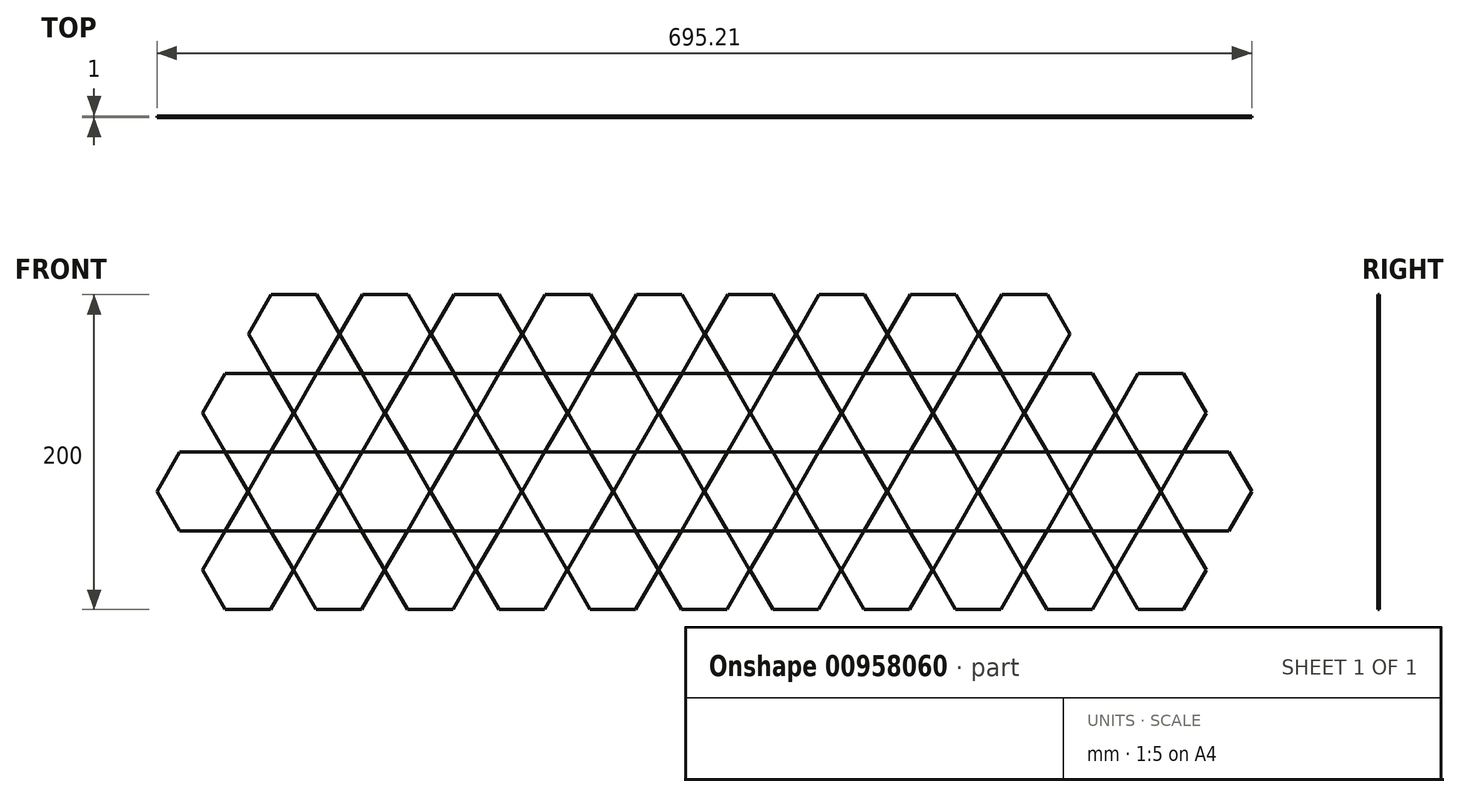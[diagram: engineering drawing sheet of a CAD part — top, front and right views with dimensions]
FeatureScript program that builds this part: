
annotation { "Feature Type Name" : "Feature", "Feature Type Description" : "" }
export const myFeature = defineFeature(function(context is Context, id is Id, definition is map)
    precondition{}
    {
        {
            var Q0;
            Q0=qCreatedBy(makeId("Front.planeOp"),FACE);
            var sketch = newSketch(context, id + "F0", { "sketchPlane" : qUnion([Q0])});
            skLineSegment(sketch, "E0.bottom", {"start": v(0, 0) * mm, "end": v(820, 0) * mm});
            skLineSegment(sketch, "E0.top", {"start": v(0, 215) * mm, "end": v(820, 215) * mm});
            skLineSegment(sketch, "E0.left", {"start": v(0, 0) * mm, "end": v(0, 215) * mm});
            skLineSegment(sketch, "E0.right", {"start": v(820, 0) * mm, "end": v(820, 215) * mm});
            skCircle(sketch, "E1.cCircle", {"center": v(39.24, 190) * mm, "radius": 25 * mm, "construction": true});
            skLineSegment(sketch, "E1.0", {"start": v(24.8, 215) * mm, "end": v(53.67, 215) * mm});
            skLineSegment(sketch, "E1.1", {"start": v(53.67, 215) * mm, "end": v(68.1, 190) * mm});
            skLineSegment(sketch, "E1.2", {"start": v(68.1, 190) * mm, "end": v(53.67, 165) * mm});
            skLineSegment(sketch, "E1.3", {"start": v(53.67, 165) * mm, "end": v(24.8, 165) * mm});
            skLineSegment(sketch, "E1.4", {"start": v(24.8, 165) * mm, "end": v(10.37, 190) * mm});
            skLineSegment(sketch, "E1.5", {"start": v(10.37, 190) * mm, "end": v(24.8, 215) * mm});
            skPoint(sketch, "E1.0.midPoint", {"position": v(39.24, 215) * mm});
            skCircle(sketch, "E2.cCircle", {"center": v(68.1, 140) * mm, "radius": 25 * mm, "construction": true});
            skLineSegment(sketch, "E2.0", {"start": v(53.67, 165) * mm, "end": v(82.54, 165) * mm});
            skLineSegment(sketch, "E2.1", {"start": v(82.54, 165) * mm, "end": v(96.97, 140) * mm});
            skLineSegment(sketch, "E2.2", {"start": v(96.97, 140) * mm, "end": v(82.54, 115) * mm});
            skLineSegment(sketch, "E2.3", {"start": v(82.54, 115) * mm, "end": v(53.67, 115) * mm});
            skLineSegment(sketch, "E2.4", {"start": v(53.67, 115) * mm, "end": v(39.24, 140) * mm});
            skLineSegment(sketch, "E2.5", {"start": v(39.24, 140) * mm, "end": v(53.67, 165) * mm});
            skPoint(sketch, "E2.0.midPoint", {"position": v(68.1, 165) * mm});
            skCircle(sketch, "E3.cCircle", {"center": v(96.97, 90) * mm, "radius": 25 * mm, "construction": true});
            skLineSegment(sketch, "E3.0", {"start": v(82.54, 115) * mm, "end": v(111.4, 115) * mm});
            skLineSegment(sketch, "E3.1", {"start": v(111.4, 115) * mm, "end": v(125.84, 90) * mm});
            skLineSegment(sketch, "E3.2", {"start": v(125.84, 90) * mm, "end": v(111.4, 65) * mm});
            skLineSegment(sketch, "E3.3", {"start": v(111.4, 65) * mm, "end": v(82.54, 65) * mm});
            skLineSegment(sketch, "E3.4", {"start": v(82.54, 65) * mm, "end": v(68.1, 90) * mm});
            skLineSegment(sketch, "E3.5", {"start": v(68.1, 90) * mm, "end": v(82.54, 115) * mm});
            skCircle(sketch, "E4.cCircle", {"center": v(125.84, 40) * mm, "radius": 25 * mm, "construction": true});
            skLineSegment(sketch, "E4.0", {"start": v(111.4, 65) * mm, "end": v(140.27, 65) * mm});
            skLineSegment(sketch, "E4.1", {"start": v(140.27, 65) * mm, "end": v(154.7, 40) * mm});
            skLineSegment(sketch, "E4.2", {"start": v(154.7, 40) * mm, "end": v(140.27, 15) * mm});
            skLineSegment(sketch, "E4.3", {"start": v(140.27, 15) * mm, "end": v(111.4, 15) * mm});
            skLineSegment(sketch, "E4.4", {"start": v(111.4, 15) * mm, "end": v(96.97, 40) * mm});
            skLineSegment(sketch, "E4.5", {"start": v(96.97, 40) * mm, "end": v(111.4, 65) * mm});
            skLineSegment(sketch, "E5", {"start": v(10.37, 190) * mm, "end": v(96.97, 40) * mm});
            skLineSegment(sketch, "E6.1.0.0", {"start": v(198.27, 65) * mm, "end": v(212.7, 40) * mm});
            skCircle(sketch, "E6.1.0.1", {"center": v(126.1, 140) * mm, "radius": 25 * mm, "construction": true});
            skLineSegment(sketch, "E6.1.0.2", {"start": v(126.1, 190) * mm, "end": v(111.67, 165) * mm});
            skPoint(sketch, "E6.1.0.4", {"position": v(97.24, 215) * mm});
            skLineSegment(sketch, "E6.1.0.5", {"start": v(111.67, 115) * mm, "end": v(97.24, 140) * mm});
            skLineSegment(sketch, "E6.1.0.6", {"start": v(140.54, 65) * mm, "end": v(126.1, 90) * mm});
            skLineSegment(sketch, "E6.1.0.7", {"start": v(140.54, 165) * mm, "end": v(154.97, 140) * mm});
            skLineSegment(sketch, "E6.1.0.8", {"start": v(111.67, 215) * mm, "end": v(126.1, 190) * mm});
            skCircle(sketch, "E6.1.0.9", {"center": v(154.97, 90) * mm, "radius": 25 * mm, "construction": true});
            skCircle(sketch, "E6.1.0.10", {"center": v(97.24, 190) * mm, "radius": 25 * mm, "construction": true});
            skLineSegment(sketch, "E6.1.0.11", {"start": v(82.8, 165) * mm, "end": v(68.37, 190) * mm});
            skLineSegment(sketch, "E6.1.0.12", {"start": v(97.24, 140) * mm, "end": v(111.67, 165) * mm});
            skLineSegment(sketch, "E6.1.0.13", {"start": v(183.84, 90) * mm, "end": v(169.4, 65) * mm});
            skLineSegment(sketch, "E6.1.0.14", {"start": v(68.37, 190) * mm, "end": v(154.97, 40) * mm});
            skPoint(sketch, "E6.1.0.15", {"position": v(126.1, 165) * mm});
            skCircle(sketch, "E6.1.0.16", {"center": v(183.84, 40) * mm, "radius": 25 * mm, "construction": true});
            skLineSegment(sketch, "E6.1.0.17", {"start": v(140.54, 115) * mm, "end": v(111.67, 115) * mm});
            skLineSegment(sketch, "E6.1.0.18", {"start": v(198.27, 15) * mm, "end": v(169.4, 15) * mm});
            skLineSegment(sketch, "E6.1.0.19", {"start": v(68.37, 190) * mm, "end": v(82.8, 215) * mm});
            skLineSegment(sketch, "E6.1.0.20", {"start": v(126.1, 90) * mm, "end": v(140.54, 115) * mm});
            skLineSegment(sketch, "E6.1.0.21", {"start": v(111.67, 165) * mm, "end": v(82.8, 165) * mm});
            skLineSegment(sketch, "E6.1.0.22", {"start": v(111.67, 165) * mm, "end": v(140.54, 165) * mm});
            skLineSegment(sketch, "E6.1.0.23", {"start": v(169.4, 65) * mm, "end": v(198.27, 65) * mm});
            skLineSegment(sketch, "E6.1.0.24", {"start": v(140.54, 115) * mm, "end": v(169.4, 115) * mm});
            skLineSegment(sketch, "E6.1.0.25", {"start": v(169.4, 115) * mm, "end": v(183.84, 90) * mm});
            skLineSegment(sketch, "E6.1.0.26", {"start": v(212.7, 40) * mm, "end": v(198.27, 15) * mm});
            skLineSegment(sketch, "E6.1.0.27", {"start": v(169.4, 15) * mm, "end": v(154.97, 40) * mm});
            skLineSegment(sketch, "E6.1.0.28", {"start": v(169.4, 65) * mm, "end": v(140.54, 65) * mm});
            skLineSegment(sketch, "E6.1.0.29", {"start": v(154.97, 140) * mm, "end": v(140.54, 115) * mm});
            skLineSegment(sketch, "E6.1.0.30", {"start": v(154.97, 40) * mm, "end": v(169.4, 65) * mm});
            skLineSegment(sketch, "E6.1.0.31", {"start": v(82.8, 215) * mm, "end": v(111.67, 215) * mm});
            skLineSegment(sketch, "E6.2.0.0", {"start": v(256.27, 65) * mm, "end": v(270.7, 40) * mm});
            skCircle(sketch, "E6.2.0.1", {"center": v(184.1, 140) * mm, "radius": 25 * mm, "construction": true});
            skLineSegment(sketch, "E6.2.0.2", {"start": v(184.1, 190) * mm, "end": v(169.67, 165) * mm});
            skPoint(sketch, "E6.2.0.4", {"position": v(155.24, 215) * mm});
            skLineSegment(sketch, "E6.2.0.5", {"start": v(169.67, 115) * mm, "end": v(155.24, 140) * mm});
            skLineSegment(sketch, "E6.2.0.6", {"start": v(198.54, 65) * mm, "end": v(184.1, 90) * mm});
            skLineSegment(sketch, "E6.2.0.7", {"start": v(198.54, 165) * mm, "end": v(212.97, 140) * mm});
            skLineSegment(sketch, "E6.2.0.8", {"start": v(169.67, 215) * mm, "end": v(184.1, 190) * mm});
            skCircle(sketch, "E6.2.0.9", {"center": v(212.97, 90) * mm, "radius": 25 * mm, "construction": true});
            skCircle(sketch, "E6.2.0.10", {"center": v(155.24, 190) * mm, "radius": 25 * mm, "construction": true});
            skLineSegment(sketch, "E6.2.0.11", {"start": v(140.8, 165) * mm, "end": v(126.37, 190) * mm});
            skLineSegment(sketch, "E6.2.0.12", {"start": v(155.24, 140) * mm, "end": v(169.67, 165) * mm});
            skLineSegment(sketch, "E6.2.0.13", {"start": v(241.84, 90) * mm, "end": v(227.4, 65) * mm});
            skLineSegment(sketch, "E6.2.0.14", {"start": v(126.37, 190) * mm, "end": v(212.97, 40) * mm});
            skPoint(sketch, "E6.2.0.15", {"position": v(184.1, 165) * mm});
            skCircle(sketch, "E6.2.0.16", {"center": v(241.84, 40) * mm, "radius": 25 * mm, "construction": true});
            skLineSegment(sketch, "E6.2.0.17", {"start": v(198.54, 115) * mm, "end": v(169.67, 115) * mm});
            skLineSegment(sketch, "E6.2.0.18", {"start": v(256.27, 15) * mm, "end": v(227.4, 15) * mm});
            skLineSegment(sketch, "E6.2.0.19", {"start": v(126.37, 190) * mm, "end": v(140.8, 215) * mm});
            skLineSegment(sketch, "E6.2.0.20", {"start": v(184.1, 90) * mm, "end": v(198.54, 115) * mm});
            skLineSegment(sketch, "E6.2.0.21", {"start": v(169.67, 165) * mm, "end": v(140.8, 165) * mm});
            skLineSegment(sketch, "E6.2.0.22", {"start": v(169.67, 165) * mm, "end": v(198.54, 165) * mm});
            skLineSegment(sketch, "E6.2.0.23", {"start": v(227.4, 65) * mm, "end": v(256.27, 65) * mm});
            skLineSegment(sketch, "E6.2.0.24", {"start": v(198.54, 115) * mm, "end": v(227.4, 115) * mm});
            skLineSegment(sketch, "E6.2.0.25", {"start": v(227.4, 115) * mm, "end": v(241.84, 90) * mm});
            skLineSegment(sketch, "E6.2.0.26", {"start": v(270.7, 40) * mm, "end": v(256.27, 15) * mm});
            skLineSegment(sketch, "E6.2.0.27", {"start": v(227.4, 15) * mm, "end": v(212.97, 40) * mm});
            skLineSegment(sketch, "E6.2.0.28", {"start": v(227.4, 65) * mm, "end": v(198.54, 65) * mm});
            skLineSegment(sketch, "E6.2.0.29", {"start": v(212.97, 140) * mm, "end": v(198.54, 115) * mm});
            skLineSegment(sketch, "E6.2.0.30", {"start": v(212.97, 40) * mm, "end": v(227.4, 65) * mm});
            skLineSegment(sketch, "E6.2.0.31", {"start": v(140.8, 215) * mm, "end": v(169.67, 215) * mm});
            skLineSegment(sketch, "E6.3.0.0", {"start": v(314.27, 65) * mm, "end": v(328.7, 40) * mm});
            skCircle(sketch, "E6.3.0.1", {"center": v(242.1, 140) * mm, "radius": 25 * mm, "construction": true});
            skLineSegment(sketch, "E6.3.0.2", {"start": v(242.1, 190) * mm, "end": v(227.67, 165) * mm});
            skPoint(sketch, "E6.3.0.4", {"position": v(213.24, 215) * mm});
            skLineSegment(sketch, "E6.3.0.5", {"start": v(227.67, 115) * mm, "end": v(213.24, 140) * mm});
            skLineSegment(sketch, "E6.3.0.6", {"start": v(256.54, 65) * mm, "end": v(242.1, 90) * mm});
            skLineSegment(sketch, "E6.3.0.7", {"start": v(256.54, 165) * mm, "end": v(270.97, 140) * mm});
            skLineSegment(sketch, "E6.3.0.8", {"start": v(227.67, 215) * mm, "end": v(242.1, 190) * mm});
            skCircle(sketch, "E6.3.0.9", {"center": v(270.97, 90) * mm, "radius": 25 * mm, "construction": true});
            skCircle(sketch, "E6.3.0.10", {"center": v(213.24, 190) * mm, "radius": 25 * mm, "construction": true});
            skLineSegment(sketch, "E6.3.0.11", {"start": v(198.8, 165) * mm, "end": v(184.37, 190) * mm});
            skLineSegment(sketch, "E6.3.0.12", {"start": v(213.24, 140) * mm, "end": v(227.67, 165) * mm});
            skLineSegment(sketch, "E6.3.0.13", {"start": v(299.84, 90) * mm, "end": v(285.4, 65) * mm});
            skLineSegment(sketch, "E6.3.0.14", {"start": v(184.37, 190) * mm, "end": v(270.97, 40) * mm});
            skPoint(sketch, "E6.3.0.15", {"position": v(242.1, 165) * mm});
            skCircle(sketch, "E6.3.0.16", {"center": v(299.84, 40) * mm, "radius": 25 * mm, "construction": true});
            skLineSegment(sketch, "E6.3.0.17", {"start": v(256.54, 115) * mm, "end": v(227.67, 115) * mm});
            skLineSegment(sketch, "E6.3.0.18", {"start": v(314.27, 15) * mm, "end": v(285.4, 15) * mm});
            skLineSegment(sketch, "E6.3.0.19", {"start": v(184.37, 190) * mm, "end": v(198.8, 215) * mm});
            skLineSegment(sketch, "E6.3.0.20", {"start": v(242.1, 90) * mm, "end": v(256.54, 115) * mm});
            skLineSegment(sketch, "E6.3.0.21", {"start": v(227.67, 165) * mm, "end": v(198.8, 165) * mm});
            skLineSegment(sketch, "E6.3.0.22", {"start": v(227.67, 165) * mm, "end": v(256.54, 165) * mm});
            skLineSegment(sketch, "E6.3.0.23", {"start": v(285.4, 65) * mm, "end": v(314.27, 65) * mm});
            skLineSegment(sketch, "E6.3.0.24", {"start": v(256.54, 115) * mm, "end": v(285.4, 115) * mm});
            skLineSegment(sketch, "E6.3.0.25", {"start": v(285.4, 115) * mm, "end": v(299.84, 90) * mm});
            skLineSegment(sketch, "E6.3.0.26", {"start": v(328.7, 40) * mm, "end": v(314.27, 15) * mm});
            skLineSegment(sketch, "E6.3.0.27", {"start": v(285.4, 15) * mm, "end": v(270.97, 40) * mm});
            skLineSegment(sketch, "E6.3.0.28", {"start": v(285.4, 65) * mm, "end": v(256.54, 65) * mm});
            skLineSegment(sketch, "E6.3.0.29", {"start": v(270.97, 140) * mm, "end": v(256.54, 115) * mm});
            skLineSegment(sketch, "E6.3.0.30", {"start": v(270.97, 40) * mm, "end": v(285.4, 65) * mm});
            skLineSegment(sketch, "E6.3.0.31", {"start": v(198.8, 215) * mm, "end": v(227.67, 215) * mm});
            skLineSegment(sketch, "E6.4.0.0", {"start": v(372.27, 65) * mm, "end": v(386.7, 40) * mm});
            skCircle(sketch, "E6.4.0.1", {"center": v(300.1, 140) * mm, "radius": 25 * mm, "construction": true});
            skLineSegment(sketch, "E6.4.0.2", {"start": v(300.1, 190) * mm, "end": v(285.67, 165) * mm});
            skPoint(sketch, "E6.4.0.4", {"position": v(271.24, 215) * mm});
            skLineSegment(sketch, "E6.4.0.5", {"start": v(285.67, 115) * mm, "end": v(271.24, 140) * mm});
            skLineSegment(sketch, "E6.4.0.6", {"start": v(314.54, 65) * mm, "end": v(300.1, 90) * mm});
            skLineSegment(sketch, "E6.4.0.7", {"start": v(314.54, 165) * mm, "end": v(328.97, 140) * mm});
            skLineSegment(sketch, "E6.4.0.8", {"start": v(285.67, 215) * mm, "end": v(300.1, 190) * mm});
            skCircle(sketch, "E6.4.0.9", {"center": v(328.97, 90) * mm, "radius": 25 * mm, "construction": true});
            skCircle(sketch, "E6.4.0.10", {"center": v(271.24, 190) * mm, "radius": 25 * mm, "construction": true});
            skLineSegment(sketch, "E6.4.0.11", {"start": v(256.8, 165) * mm, "end": v(242.37, 190) * mm});
            skLineSegment(sketch, "E6.4.0.12", {"start": v(271.24, 140) * mm, "end": v(285.67, 165) * mm});
            skLineSegment(sketch, "E6.4.0.13", {"start": v(357.84, 90) * mm, "end": v(343.4, 65) * mm});
            skLineSegment(sketch, "E6.4.0.14", {"start": v(242.37, 190) * mm, "end": v(328.97, 40) * mm});
            skPoint(sketch, "E6.4.0.15", {"position": v(300.1, 165) * mm});
            skCircle(sketch, "E6.4.0.16", {"center": v(357.84, 40) * mm, "radius": 25 * mm, "construction": true});
            skLineSegment(sketch, "E6.4.0.17", {"start": v(314.54, 115) * mm, "end": v(285.67, 115) * mm});
            skLineSegment(sketch, "E6.4.0.18", {"start": v(372.27, 15) * mm, "end": v(343.4, 15) * mm});
            skLineSegment(sketch, "E6.4.0.19", {"start": v(242.37, 190) * mm, "end": v(256.8, 215) * mm});
            skLineSegment(sketch, "E6.4.0.20", {"start": v(300.1, 90) * mm, "end": v(314.54, 115) * mm});
            skLineSegment(sketch, "E6.4.0.21", {"start": v(285.67, 165) * mm, "end": v(256.8, 165) * mm});
            skLineSegment(sketch, "E6.4.0.22", {"start": v(285.67, 165) * mm, "end": v(314.54, 165) * mm});
            skLineSegment(sketch, "E6.4.0.23", {"start": v(343.4, 65) * mm, "end": v(372.27, 65) * mm});
            skLineSegment(sketch, "E6.4.0.24", {"start": v(314.54, 115) * mm, "end": v(343.4, 115) * mm});
            skLineSegment(sketch, "E6.4.0.25", {"start": v(343.4, 115) * mm, "end": v(357.84, 90) * mm});
            skLineSegment(sketch, "E6.4.0.26", {"start": v(386.7, 40) * mm, "end": v(372.27, 15) * mm});
            skLineSegment(sketch, "E6.4.0.27", {"start": v(343.4, 15) * mm, "end": v(328.97, 40) * mm});
            skLineSegment(sketch, "E6.4.0.28", {"start": v(343.4, 65) * mm, "end": v(314.54, 65) * mm});
            skLineSegment(sketch, "E6.4.0.29", {"start": v(328.97, 140) * mm, "end": v(314.54, 115) * mm});
            skLineSegment(sketch, "E6.4.0.30", {"start": v(328.97, 40) * mm, "end": v(343.4, 65) * mm});
            skLineSegment(sketch, "E6.4.0.31", {"start": v(256.8, 215) * mm, "end": v(285.67, 215) * mm});
            skLineSegment(sketch, "E6.5.0.0", {"start": v(430.27, 65) * mm, "end": v(444.7, 40) * mm});
            skCircle(sketch, "E6.5.0.1", {"center": v(358.1, 140) * mm, "radius": 25 * mm, "construction": true});
            skLineSegment(sketch, "E6.5.0.2", {"start": v(358.1, 190) * mm, "end": v(343.67, 165) * mm});
            skPoint(sketch, "E6.5.0.4", {"position": v(329.24, 215) * mm});
            skLineSegment(sketch, "E6.5.0.5", {"start": v(343.67, 115) * mm, "end": v(329.24, 140) * mm});
            skLineSegment(sketch, "E6.5.0.6", {"start": v(372.54, 65) * mm, "end": v(358.1, 90) * mm});
            skLineSegment(sketch, "E6.5.0.7", {"start": v(372.54, 165) * mm, "end": v(386.97, 140) * mm});
            skLineSegment(sketch, "E6.5.0.8", {"start": v(343.67, 215) * mm, "end": v(358.1, 190) * mm});
            skCircle(sketch, "E6.5.0.9", {"center": v(386.97, 90) * mm, "radius": 25 * mm, "construction": true});
            skCircle(sketch, "E6.5.0.10", {"center": v(329.24, 190) * mm, "radius": 25 * mm, "construction": true});
            skLineSegment(sketch, "E6.5.0.11", {"start": v(314.8, 165) * mm, "end": v(300.37, 190) * mm});
            skLineSegment(sketch, "E6.5.0.12", {"start": v(329.24, 140) * mm, "end": v(343.67, 165) * mm});
            skLineSegment(sketch, "E6.5.0.13", {"start": v(415.84, 90) * mm, "end": v(401.4, 65) * mm});
            skLineSegment(sketch, "E6.5.0.14", {"start": v(300.37, 190) * mm, "end": v(386.97, 40) * mm});
            skPoint(sketch, "E6.5.0.15", {"position": v(358.1, 165) * mm});
            skCircle(sketch, "E6.5.0.16", {"center": v(415.84, 40) * mm, "radius": 25 * mm, "construction": true});
            skLineSegment(sketch, "E6.5.0.17", {"start": v(372.54, 115) * mm, "end": v(343.67, 115) * mm});
            skLineSegment(sketch, "E6.5.0.18", {"start": v(430.27, 15) * mm, "end": v(401.4, 15) * mm});
            skLineSegment(sketch, "E6.5.0.19", {"start": v(300.37, 190) * mm, "end": v(314.8, 215) * mm});
            skLineSegment(sketch, "E6.5.0.20", {"start": v(358.1, 90) * mm, "end": v(372.54, 115) * mm});
            skLineSegment(sketch, "E6.5.0.21", {"start": v(343.67, 165) * mm, "end": v(314.8, 165) * mm});
            skLineSegment(sketch, "E6.5.0.22", {"start": v(343.67, 165) * mm, "end": v(372.54, 165) * mm});
            skLineSegment(sketch, "E6.5.0.23", {"start": v(401.4, 65) * mm, "end": v(430.27, 65) * mm});
            skLineSegment(sketch, "E6.5.0.24", {"start": v(372.54, 115) * mm, "end": v(401.4, 115) * mm});
            skLineSegment(sketch, "E6.5.0.25", {"start": v(401.4, 115) * mm, "end": v(415.84, 90) * mm});
            skLineSegment(sketch, "E6.5.0.26", {"start": v(444.7, 40) * mm, "end": v(430.27, 15) * mm});
            skLineSegment(sketch, "E6.5.0.27", {"start": v(401.4, 15) * mm, "end": v(386.97, 40) * mm});
            skLineSegment(sketch, "E6.5.0.28", {"start": v(401.4, 65) * mm, "end": v(372.54, 65) * mm});
            skLineSegment(sketch, "E6.5.0.29", {"start": v(386.97, 140) * mm, "end": v(372.54, 115) * mm});
            skLineSegment(sketch, "E6.5.0.30", {"start": v(386.97, 40) * mm, "end": v(401.4, 65) * mm});
            skLineSegment(sketch, "E6.5.0.31", {"start": v(314.8, 215) * mm, "end": v(343.67, 215) * mm});
            skLineSegment(sketch, "E6.6.0.0", {"start": v(488.27, 65) * mm, "end": v(502.7, 40) * mm});
            skCircle(sketch, "E6.6.0.1", {"center": v(416.1, 140) * mm, "radius": 25 * mm, "construction": true});
            skLineSegment(sketch, "E6.6.0.2", {"start": v(416.1, 190) * mm, "end": v(401.67, 165) * mm});
            skPoint(sketch, "E6.6.0.4", {"position": v(387.24, 215) * mm});
            skLineSegment(sketch, "E6.6.0.5", {"start": v(401.67, 115) * mm, "end": v(387.24, 140) * mm});
            skLineSegment(sketch, "E6.6.0.6", {"start": v(430.54, 65) * mm, "end": v(416.1, 90) * mm});
            skLineSegment(sketch, "E6.6.0.7", {"start": v(430.54, 165) * mm, "end": v(444.97, 140) * mm});
            skLineSegment(sketch, "E6.6.0.8", {"start": v(401.67, 215) * mm, "end": v(416.1, 190) * mm});
            skCircle(sketch, "E6.6.0.9", {"center": v(444.97, 90) * mm, "radius": 25 * mm, "construction": true});
            skCircle(sketch, "E6.6.0.10", {"center": v(387.24, 190) * mm, "radius": 25 * mm, "construction": true});
            skLineSegment(sketch, "E6.6.0.11", {"start": v(372.8, 165) * mm, "end": v(358.37, 190) * mm});
            skLineSegment(sketch, "E6.6.0.12", {"start": v(387.24, 140) * mm, "end": v(401.67, 165) * mm});
            skLineSegment(sketch, "E6.6.0.13", {"start": v(473.84, 90) * mm, "end": v(459.4, 65) * mm});
            skLineSegment(sketch, "E6.6.0.14", {"start": v(358.37, 190) * mm, "end": v(444.97, 40) * mm});
            skPoint(sketch, "E6.6.0.15", {"position": v(416.1, 165) * mm});
            skCircle(sketch, "E6.6.0.16", {"center": v(473.84, 40) * mm, "radius": 25 * mm, "construction": true});
            skLineSegment(sketch, "E6.6.0.17", {"start": v(430.54, 115) * mm, "end": v(401.67, 115) * mm});
            skLineSegment(sketch, "E6.6.0.18", {"start": v(488.27, 15) * mm, "end": v(459.4, 15) * mm});
            skLineSegment(sketch, "E6.6.0.19", {"start": v(358.37, 190) * mm, "end": v(372.8, 215) * mm});
            skLineSegment(sketch, "E6.6.0.20", {"start": v(416.1, 90) * mm, "end": v(430.54, 115) * mm});
            skLineSegment(sketch, "E6.6.0.21", {"start": v(401.67, 165) * mm, "end": v(372.8, 165) * mm});
            skLineSegment(sketch, "E6.6.0.22", {"start": v(401.67, 165) * mm, "end": v(430.54, 165) * mm});
            skLineSegment(sketch, "E6.6.0.23", {"start": v(459.4, 65) * mm, "end": v(488.27, 65) * mm});
            skLineSegment(sketch, "E6.6.0.24", {"start": v(430.54, 115) * mm, "end": v(459.4, 115) * mm});
            skLineSegment(sketch, "E6.6.0.25", {"start": v(459.4, 115) * mm, "end": v(473.84, 90) * mm});
            skLineSegment(sketch, "E6.6.0.26", {"start": v(502.7, 40) * mm, "end": v(488.27, 15) * mm});
            skLineSegment(sketch, "E6.6.0.27", {"start": v(459.4, 15) * mm, "end": v(444.97, 40) * mm});
            skLineSegment(sketch, "E6.6.0.28", {"start": v(459.4, 65) * mm, "end": v(430.54, 65) * mm});
            skLineSegment(sketch, "E6.6.0.29", {"start": v(444.97, 140) * mm, "end": v(430.54, 115) * mm});
            skLineSegment(sketch, "E6.6.0.30", {"start": v(444.97, 40) * mm, "end": v(459.4, 65) * mm});
            skLineSegment(sketch, "E6.6.0.31", {"start": v(372.8, 215) * mm, "end": v(401.67, 215) * mm});
            skLineSegment(sketch, "E6.7.0.0", {"start": v(546.27, 65) * mm, "end": v(560.7, 40) * mm});
            skCircle(sketch, "E6.7.0.1", {"center": v(474.1, 140) * mm, "radius": 25 * mm, "construction": true});
            skLineSegment(sketch, "E6.7.0.2", {"start": v(474.1, 190) * mm, "end": v(459.67, 165) * mm});
            skPoint(sketch, "E6.7.0.4", {"position": v(445.24, 215) * mm});
            skLineSegment(sketch, "E6.7.0.5", {"start": v(459.67, 115) * mm, "end": v(445.24, 140) * mm});
            skLineSegment(sketch, "E6.7.0.6", {"start": v(488.54, 65) * mm, "end": v(474.1, 90) * mm});
            skLineSegment(sketch, "E6.7.0.7", {"start": v(488.54, 165) * mm, "end": v(502.97, 140) * mm});
            skLineSegment(sketch, "E6.7.0.8", {"start": v(459.67, 215) * mm, "end": v(474.1, 190) * mm});
            skCircle(sketch, "E6.7.0.9", {"center": v(502.97, 90) * mm, "radius": 25 * mm, "construction": true});
            skCircle(sketch, "E6.7.0.10", {"center": v(445.24, 190) * mm, "radius": 25 * mm, "construction": true});
            skLineSegment(sketch, "E6.7.0.11", {"start": v(430.8, 165) * mm, "end": v(416.37, 190) * mm});
            skLineSegment(sketch, "E6.7.0.12", {"start": v(445.24, 140) * mm, "end": v(459.67, 165) * mm});
            skLineSegment(sketch, "E6.7.0.13", {"start": v(531.84, 90) * mm, "end": v(517.4, 65) * mm});
            skLineSegment(sketch, "E6.7.0.14", {"start": v(416.37, 190) * mm, "end": v(502.97, 40) * mm});
            skPoint(sketch, "E6.7.0.15", {"position": v(474.1, 165) * mm});
            skCircle(sketch, "E6.7.0.16", {"center": v(531.84, 40) * mm, "radius": 25 * mm, "construction": true});
            skLineSegment(sketch, "E6.7.0.17", {"start": v(488.54, 115) * mm, "end": v(459.67, 115) * mm});
            skLineSegment(sketch, "E6.7.0.18", {"start": v(546.27, 15) * mm, "end": v(517.4, 15) * mm});
            skLineSegment(sketch, "E6.7.0.19", {"start": v(416.37, 190) * mm, "end": v(430.8, 215) * mm});
            skLineSegment(sketch, "E6.7.0.20", {"start": v(474.1, 90) * mm, "end": v(488.54, 115) * mm});
            skLineSegment(sketch, "E6.7.0.21", {"start": v(459.67, 165) * mm, "end": v(430.8, 165) * mm});
            skLineSegment(sketch, "E6.7.0.22", {"start": v(459.67, 165) * mm, "end": v(488.54, 165) * mm});
            skLineSegment(sketch, "E6.7.0.23", {"start": v(517.4, 65) * mm, "end": v(546.27, 65) * mm});
            skLineSegment(sketch, "E6.7.0.24", {"start": v(488.54, 115) * mm, "end": v(517.4, 115) * mm});
            skLineSegment(sketch, "E6.7.0.25", {"start": v(517.4, 115) * mm, "end": v(531.84, 90) * mm});
            skLineSegment(sketch, "E6.7.0.26", {"start": v(560.7, 40) * mm, "end": v(546.27, 15) * mm});
            skLineSegment(sketch, "E6.7.0.27", {"start": v(517.4, 15) * mm, "end": v(502.97, 40) * mm});
            skLineSegment(sketch, "E6.7.0.28", {"start": v(517.4, 65) * mm, "end": v(488.54, 65) * mm});
            skLineSegment(sketch, "E6.7.0.29", {"start": v(502.97, 140) * mm, "end": v(488.54, 115) * mm});
            skLineSegment(sketch, "E6.7.0.30", {"start": v(502.97, 40) * mm, "end": v(517.4, 65) * mm});
            skLineSegment(sketch, "E6.7.0.31", {"start": v(430.8, 215) * mm, "end": v(459.67, 215) * mm});
            skLineSegment(sketch, "E6.8.0.0", {"start": v(604.27, 65) * mm, "end": v(618.7, 40) * mm});
            skCircle(sketch, "E6.8.0.1", {"center": v(532.1, 140) * mm, "radius": 25 * mm, "construction": true});
            skLineSegment(sketch, "E6.8.0.2", {"start": v(532.1, 190) * mm, "end": v(517.67, 165) * mm});
            skPoint(sketch, "E6.8.0.4", {"position": v(503.24, 215) * mm});
            skLineSegment(sketch, "E6.8.0.5", {"start": v(517.67, 115) * mm, "end": v(503.24, 140) * mm});
            skLineSegment(sketch, "E6.8.0.6", {"start": v(546.54, 65) * mm, "end": v(532.1, 90) * mm});
            skLineSegment(sketch, "E6.8.0.7", {"start": v(546.54, 165) * mm, "end": v(560.97, 140) * mm});
            skLineSegment(sketch, "E6.8.0.8", {"start": v(517.67, 215) * mm, "end": v(532.1, 190) * mm});
            skCircle(sketch, "E6.8.0.9", {"center": v(560.97, 90) * mm, "radius": 25 * mm, "construction": true});
            skCircle(sketch, "E6.8.0.10", {"center": v(503.24, 190) * mm, "radius": 25 * mm, "construction": true});
            skLineSegment(sketch, "E6.8.0.11", {"start": v(488.8, 165) * mm, "end": v(474.37, 190) * mm});
            skLineSegment(sketch, "E6.8.0.12", {"start": v(503.24, 140) * mm, "end": v(517.67, 165) * mm});
            skLineSegment(sketch, "E6.8.0.13", {"start": v(589.84, 90) * mm, "end": v(575.4, 65) * mm});
            skLineSegment(sketch, "E6.8.0.14", {"start": v(474.37, 190) * mm, "end": v(560.97, 40) * mm});
            skPoint(sketch, "E6.8.0.15", {"position": v(532.1, 165) * mm});
            skCircle(sketch, "E6.8.0.16", {"center": v(589.84, 40) * mm, "radius": 25 * mm, "construction": true});
            skLineSegment(sketch, "E6.8.0.17", {"start": v(546.54, 115) * mm, "end": v(517.67, 115) * mm});
            skLineSegment(sketch, "E6.8.0.18", {"start": v(604.27, 15) * mm, "end": v(575.4, 15) * mm});
            skLineSegment(sketch, "E6.8.0.19", {"start": v(474.37, 190) * mm, "end": v(488.8, 215) * mm});
            skLineSegment(sketch, "E6.8.0.20", {"start": v(532.1, 90) * mm, "end": v(546.54, 115) * mm});
            skLineSegment(sketch, "E6.8.0.21", {"start": v(517.67, 165) * mm, "end": v(488.8, 165) * mm});
            skLineSegment(sketch, "E6.8.0.22", {"start": v(517.67, 165) * mm, "end": v(546.54, 165) * mm});
            skLineSegment(sketch, "E6.8.0.23", {"start": v(575.4, 65) * mm, "end": v(604.27, 65) * mm});
            skLineSegment(sketch, "E6.8.0.24", {"start": v(546.54, 115) * mm, "end": v(575.4, 115) * mm});
            skLineSegment(sketch, "E6.8.0.25", {"start": v(575.4, 115) * mm, "end": v(589.84, 90) * mm});
            skLineSegment(sketch, "E6.8.0.26", {"start": v(618.7, 40) * mm, "end": v(604.27, 15) * mm});
            skLineSegment(sketch, "E6.8.0.27", {"start": v(575.4, 15) * mm, "end": v(560.97, 40) * mm});
            skLineSegment(sketch, "E6.8.0.28", {"start": v(575.4, 65) * mm, "end": v(546.54, 65) * mm});
            skLineSegment(sketch, "E6.8.0.29", {"start": v(560.97, 140) * mm, "end": v(546.54, 115) * mm});
            skLineSegment(sketch, "E6.8.0.30", {"start": v(560.97, 40) * mm, "end": v(575.4, 65) * mm});
            skLineSegment(sketch, "E6.8.0.31", {"start": v(488.8, 215) * mm, "end": v(517.67, 215) * mm});
            skLineSegment(sketch, "E6.9.0.0", {"start": v(662.27, 65) * mm, "end": v(676.7, 40) * mm});
            skCircle(sketch, "E6.9.0.1", {"center": v(590.1, 140) * mm, "radius": 25 * mm, "construction": true});
            skLineSegment(sketch, "E6.9.0.2", {"start": v(590.1, 190) * mm, "end": v(575.67, 165) * mm});
            skPoint(sketch, "E6.9.0.4", {"position": v(561.24, 215) * mm});
            skLineSegment(sketch, "E6.9.0.5", {"start": v(575.67, 115) * mm, "end": v(561.24, 140) * mm});
            skLineSegment(sketch, "E6.9.0.6", {"start": v(604.54, 65) * mm, "end": v(590.1, 90) * mm});
            skLineSegment(sketch, "E6.9.0.7", {"start": v(604.54, 165) * mm, "end": v(618.97, 140) * mm});
            skLineSegment(sketch, "E6.9.0.8", {"start": v(575.67, 215) * mm, "end": v(590.1, 190) * mm});
            skCircle(sketch, "E6.9.0.9", {"center": v(618.97, 90) * mm, "radius": 25 * mm, "construction": true});
            skCircle(sketch, "E6.9.0.10", {"center": v(561.24, 190) * mm, "radius": 25 * mm, "construction": true});
            skLineSegment(sketch, "E6.9.0.11", {"start": v(546.8, 165) * mm, "end": v(532.37, 190) * mm});
            skLineSegment(sketch, "E6.9.0.12", {"start": v(561.24, 140) * mm, "end": v(575.67, 165) * mm});
            skLineSegment(sketch, "E6.9.0.13", {"start": v(647.84, 90) * mm, "end": v(633.4, 65) * mm});
            skLineSegment(sketch, "E6.9.0.14", {"start": v(532.37, 190) * mm, "end": v(618.97, 40) * mm});
            skPoint(sketch, "E6.9.0.15", {"position": v(590.1, 165) * mm});
            skCircle(sketch, "E6.9.0.16", {"center": v(647.84, 40) * mm, "radius": 25 * mm, "construction": true});
            skLineSegment(sketch, "E6.9.0.17", {"start": v(604.54, 115) * mm, "end": v(575.67, 115) * mm});
            skLineSegment(sketch, "E6.9.0.18", {"start": v(662.27, 15) * mm, "end": v(633.4, 15) * mm});
            skLineSegment(sketch, "E6.9.0.19", {"start": v(532.37, 190) * mm, "end": v(546.8, 215) * mm});
            skLineSegment(sketch, "E6.9.0.20", {"start": v(590.1, 90) * mm, "end": v(604.54, 115) * mm});
            skLineSegment(sketch, "E6.9.0.21", {"start": v(575.67, 165) * mm, "end": v(546.8, 165) * mm});
            skLineSegment(sketch, "E6.9.0.22", {"start": v(575.67, 165) * mm, "end": v(604.54, 165) * mm});
            skLineSegment(sketch, "E6.9.0.23", {"start": v(633.4, 65) * mm, "end": v(662.27, 65) * mm});
            skLineSegment(sketch, "E6.9.0.24", {"start": v(604.54, 115) * mm, "end": v(633.4, 115) * mm});
            skLineSegment(sketch, "E6.9.0.25", {"start": v(633.4, 115) * mm, "end": v(647.84, 90) * mm});
            skLineSegment(sketch, "E6.9.0.26", {"start": v(676.7, 40) * mm, "end": v(662.27, 15) * mm});
            skLineSegment(sketch, "E6.9.0.27", {"start": v(633.4, 15) * mm, "end": v(618.97, 40) * mm});
            skLineSegment(sketch, "E6.9.0.28", {"start": v(633.4, 65) * mm, "end": v(604.54, 65) * mm});
            skLineSegment(sketch, "E6.9.0.29", {"start": v(618.97, 140) * mm, "end": v(604.54, 115) * mm});
            skLineSegment(sketch, "E6.9.0.30", {"start": v(618.97, 40) * mm, "end": v(633.4, 65) * mm});
            skLineSegment(sketch, "E6.9.0.31", {"start": v(546.8, 215) * mm, "end": v(575.67, 215) * mm});
            skLineSegment(sketch, "E6.direction1", {"start": v(0, 0) * mm, "end": v(58, 0) * mm, "construction": true});
            skCircle(sketch, "E7.cCircle", {"center": v(39.24, 90) * mm, "radius": 25 * mm, "construction": true});
            skLineSegment(sketch, "E7.0", {"start": v(24.8, 115) * mm, "end": v(53.67, 115) * mm});
            skLineSegment(sketch, "E7.1", {"start": v(53.67, 115) * mm, "end": v(68.1, 90) * mm});
            skLineSegment(sketch, "E7.2", {"start": v(68.1, 90) * mm, "end": v(53.67, 65) * mm});
            skLineSegment(sketch, "E7.3", {"start": v(53.67, 65) * mm, "end": v(24.8, 65) * mm});
            skLineSegment(sketch, "E7.4", {"start": v(24.8, 65) * mm, "end": v(10.37, 90) * mm});
            skLineSegment(sketch, "E7.5", {"start": v(10.37, 90) * mm, "end": v(24.8, 115) * mm});
            skCircle(sketch, "E8.cCircle", {"center": v(68.1, 40) * mm, "radius": 25 * mm, "construction": true});
            skLineSegment(sketch, "E8.0", {"start": v(53.67, 65) * mm, "end": v(82.54, 65) * mm});
            skLineSegment(sketch, "E8.1", {"start": v(82.54, 65) * mm, "end": v(96.97, 40) * mm});
            skLineSegment(sketch, "E8.2", {"start": v(96.97, 40) * mm, "end": v(82.54, 15) * mm});
            skLineSegment(sketch, "E8.3", {"start": v(82.54, 15) * mm, "end": v(53.67, 15) * mm});
            skLineSegment(sketch, "E8.4", {"start": v(53.67, 15) * mm, "end": v(39.24, 40) * mm});
            skLineSegment(sketch, "E8.5", {"start": v(39.24, 40) * mm, "end": v(53.67, 65) * mm});
            skCircle(sketch, "E9.cCircle", {"center": v(618.97, 190) * mm, "radius": 25 * mm, "construction": true});
            skLineSegment(sketch, "E9.0", {"start": v(604.54, 215) * mm, "end": v(633.4, 215) * mm});
            skLineSegment(sketch, "E9.1", {"start": v(633.4, 215) * mm, "end": v(647.84, 190) * mm});
            skLineSegment(sketch, "E9.2", {"start": v(647.84, 190) * mm, "end": v(633.4, 165) * mm});
            skLineSegment(sketch, "E9.3", {"start": v(633.4, 165) * mm, "end": v(604.54, 165) * mm});
            skLineSegment(sketch, "E9.4", {"start": v(604.54, 165) * mm, "end": v(590.1, 190) * mm});
            skLineSegment(sketch, "E9.5", {"start": v(590.1, 190) * mm, "end": v(604.54, 215) * mm});
            skCircle(sketch, "E10.cCircle", {"center": v(647.84, 140) * mm, "radius": 25 * mm, "construction": true});
            skLineSegment(sketch, "E10.0", {"start": v(633.4, 165) * mm, "end": v(662.27, 165) * mm});
            skLineSegment(sketch, "E10.1", {"start": v(662.27, 165) * mm, "end": v(676.7, 140) * mm});
            skLineSegment(sketch, "E10.2", {"start": v(676.7, 140) * mm, "end": v(662.27, 115) * mm});
            skLineSegment(sketch, "E10.3", {"start": v(662.27, 115) * mm, "end": v(633.4, 115) * mm});
            skLineSegment(sketch, "E10.4", {"start": v(633.4, 115) * mm, "end": v(618.97, 140) * mm});
            skLineSegment(sketch, "E10.5", {"start": v(618.97, 140) * mm, "end": v(633.4, 165) * mm});
            skCircle(sketch, "E11.cCircle", {"center": v(676.7, 90) * mm, "radius": 25 * mm, "construction": true});
            skLineSegment(sketch, "E11.0", {"start": v(662.27, 115) * mm, "end": v(691.14, 115) * mm});
            skLineSegment(sketch, "E11.1", {"start": v(691.14, 115) * mm, "end": v(705.58, 90) * mm});
            skLineSegment(sketch, "E11.2", {"start": v(705.58, 90) * mm, "end": v(691.14, 65) * mm});
            skLineSegment(sketch, "E11.3", {"start": v(691.14, 65) * mm, "end": v(662.27, 65) * mm});
            skLineSegment(sketch, "E11.4", {"start": v(662.27, 65) * mm, "end": v(647.84, 90) * mm});
            skLineSegment(sketch, "E11.5", {"start": v(647.84, 90) * mm, "end": v(662.27, 115) * mm});
            skSolve(sketch);
        }
        {
            var Q0;
            {var subQ5=sQuery(id+"F0.wireOp",EDGE,"E1.0");Q0=makeQuery(id+"F0.imprint","IMPRINT",FACE,{"disambiguationData":[TD([[makeQuery(id+"F0.imprint","IMPRINT",EDGE,{"derivedFrom":subQ5}),-1.0]])]});}
            var Q1;
            {var subQ4=sQuery(id+"F0.wireOp",EDGE,"E2.1");Q1=makeQuery(id+"F0.imprint","IMPRINT",FACE,{"disambiguationData":[TD([[makeQuery(id+"F0.imprint","IMPRINT",EDGE,{"derivedFrom":subQ4}),-1.0]])]});}
            var Q2;
            {var subQ0=sQuery(id+"F0.wireOp",EDGE,"E2.5");Q2=makeQuery(id+"F0.imprint","IMPRINT",FACE,{"disambiguationData":[TD([[makeQuery(id+"F0.imprint","IMPRINT",EDGE,{"derivedFrom":subQ0}),-1.0]])]});}
            var Q3;
            {var subQ5=sQuery(id+"F0.wireOp",EDGE,"E7.0");Q3=makeQuery(id+"F0.imprint","IMPRINT",FACE,{"disambiguationData":[TD([[makeQuery(id+"F0.imprint","IMPRINT",EDGE,{"derivedFrom":subQ5}),-1.0]])]});}
            var Q4;
            {var subQ0=sQuery(id+"F0.wireOp",EDGE,"E8.5");Q4=makeQuery(id+"F0.imprint","IMPRINT",FACE,{"disambiguationData":[TD([[makeQuery(id+"F0.imprint","IMPRINT",EDGE,{"derivedFrom":subQ0}),-1.0]])]});}
            var Q5;
            {var subQ0=sQuery(id+"F0.wireOp",EDGE,"E8.1");Q5=makeQuery(id+"F0.imprint","IMPRINT",FACE,{"disambiguationData":[TD([[makeQuery(id+"F0.imprint","IMPRINT",EDGE,{"derivedFrom":subQ0}),-1.0]])]});}
            var Q6;
            {var subQ0=sQuery(id+"F0.wireOp",EDGE,"E8.3");Q6=makeQuery(id+"F0.imprint","IMPRINT",FACE,{"disambiguationData":[TD([[makeQuery(id+"F0.imprint","IMPRINT",EDGE,{"derivedFrom":subQ0}),-1.0]])]});}
            var Q7;
            {var subQ0=sQuery(id+"F0.wireOp",EDGE,"E6.1.0.19");Q7=makeQuery(id+"F0.imprint","IMPRINT",FACE,{"disambiguationData":[TD([[makeQuery(id+"F0.imprint","IMPRINT",EDGE,{"derivedFrom":subQ0}),-1.0]])]});}
            var Q8;
            {var subQ0=sQuery(id+"F0.wireOp",EDGE,"E6.2.0.19");Q8=makeQuery(id+"F0.imprint","IMPRINT",FACE,{"disambiguationData":[TD([[makeQuery(id+"F0.imprint","IMPRINT",EDGE,{"derivedFrom":subQ0}),-1.0]])]});}
            var Q9;
            {var subQ0=sQuery(id+"F0.wireOp",EDGE,"E6.3.0.19");Q9=makeQuery(id+"F0.imprint","IMPRINT",FACE,{"disambiguationData":[TD([[makeQuery(id+"F0.imprint","IMPRINT",EDGE,{"derivedFrom":subQ0}),-1.0]])]});}
            var Q10;
            {var subQ0=sQuery(id+"F0.wireOp",EDGE,"E6.4.0.19");Q10=makeQuery(id+"F0.imprint","IMPRINT",FACE,{"disambiguationData":[TD([[makeQuery(id+"F0.imprint","IMPRINT",EDGE,{"derivedFrom":subQ0}),-1.0]])]});}
            var Q11;
            {var subQ0=sQuery(id+"F0.wireOp",EDGE,"E6.5.0.19");Q11=makeQuery(id+"F0.imprint","IMPRINT",FACE,{"disambiguationData":[TD([[makeQuery(id+"F0.imprint","IMPRINT",EDGE,{"derivedFrom":subQ0}),-1.0]])]});}
            var Q12;
            {var subQ2=sQuery(id+"F0.wireOp",EDGE,"E6.1.0.7");Q12=makeQuery(id+"F0.imprint","IMPRINT",FACE,{"disambiguationData":[TD([[makeQuery(id+"F0.imprint","IMPRINT",EDGE,{"derivedFrom":subQ2}),-1.0]])]});}
            var Q13;
            {var subQ6=sQuery(id+"F0.wireOp",EDGE,"E3.0");Q13=makeQuery(id+"F0.imprint","IMPRINT",FACE,{"disambiguationData":[TD([[makeQuery(id+"F0.imprint","IMPRINT",EDGE,{"derivedFrom":subQ6}),-1.0]])]});}
            var Q14;
            {var subQ1=sQuery(id+"F0.wireOp",EDGE,"E4.1");Q14=makeQuery(id+"F0.imprint","IMPRINT",FACE,{"disambiguationData":[TD([[makeQuery(id+"F0.imprint","IMPRINT",EDGE,{"derivedFrom":subQ1}),-1.0]])]});}
            var Q15;
            {var subQ0=sQuery(id+"F0.wireOp",EDGE,"E4.5");Q15=makeQuery(id+"F0.imprint","IMPRINT",FACE,{"disambiguationData":[TD([[makeQuery(id+"F0.imprint","IMPRINT",EDGE,{"derivedFrom":subQ0}),-1.0]])]});}
            var Q16;
            {var subQ0=sQuery(id+"F0.wireOp",EDGE,"E4.3");Q16=makeQuery(id+"F0.imprint","IMPRINT",FACE,{"disambiguationData":[TD([[makeQuery(id+"F0.imprint","IMPRINT",EDGE,{"derivedFrom":subQ0}),-1.0]])]});}
            var Q17;
            {var subQ1=sQuery(id+"F0.wireOp",EDGE,"E6.1.0.12");Q17=makeQuery(id+"F0.imprint","IMPRINT",FACE,{"disambiguationData":[TD([[makeQuery(id+"F0.imprint","IMPRINT",EDGE,{"derivedFrom":subQ1}),-1.0]])]});}
            var Q18;
            {var subQ1=sQuery(id+"F0.wireOp",EDGE,"E6.2.0.12");Q18=makeQuery(id+"F0.imprint","IMPRINT",FACE,{"disambiguationData":[TD([[makeQuery(id+"F0.imprint","IMPRINT",EDGE,{"derivedFrom":subQ1}),-1.0]])]});}
            var Q19;
            {var subQ2=sQuery(id+"F0.wireOp",EDGE,"E6.2.0.7");Q19=makeQuery(id+"F0.imprint","IMPRINT",FACE,{"disambiguationData":[TD([[makeQuery(id+"F0.imprint","IMPRINT",EDGE,{"derivedFrom":subQ2}),-1.0]])]});}
            var Q20;
            {var subQ1=sQuery(id+"F0.wireOp",EDGE,"E6.3.0.12");Q20=makeQuery(id+"F0.imprint","IMPRINT",FACE,{"disambiguationData":[TD([[makeQuery(id+"F0.imprint","IMPRINT",EDGE,{"derivedFrom":subQ1}),-1.0]])]});}
            var Q21;
            {var subQ2=sQuery(id+"F0.wireOp",EDGE,"E6.3.0.7");Q21=makeQuery(id+"F0.imprint","IMPRINT",FACE,{"disambiguationData":[TD([[makeQuery(id+"F0.imprint","IMPRINT",EDGE,{"derivedFrom":subQ2}),-1.0]])]});}
            var Q22;
            {var subQ1=sQuery(id+"F0.wireOp",EDGE,"E6.4.0.12");Q22=makeQuery(id+"F0.imprint","IMPRINT",FACE,{"disambiguationData":[TD([[makeQuery(id+"F0.imprint","IMPRINT",EDGE,{"derivedFrom":subQ1}),-1.0]])]});}
            var Q23;
            {var subQ2=sQuery(id+"F0.wireOp",EDGE,"E6.4.0.7");Q23=makeQuery(id+"F0.imprint","IMPRINT",FACE,{"disambiguationData":[TD([[makeQuery(id+"F0.imprint","IMPRINT",EDGE,{"derivedFrom":subQ2}),-1.0]])]});}
            var Q24;
            {var subQ1=sQuery(id+"F0.wireOp",EDGE,"E6.5.0.12");Q24=makeQuery(id+"F0.imprint","IMPRINT",FACE,{"disambiguationData":[TD([[makeQuery(id+"F0.imprint","IMPRINT",EDGE,{"derivedFrom":subQ1}),-1.0]])]});}
            var Q25;
            {var subQ2=sQuery(id+"F0.wireOp",EDGE,"E6.5.0.7");Q25=makeQuery(id+"F0.imprint","IMPRINT",FACE,{"disambiguationData":[TD([[makeQuery(id+"F0.imprint","IMPRINT",EDGE,{"derivedFrom":subQ2}),-1.0]])]});}
            var Q26;
            {var subQ1=sQuery(id+"F0.wireOp",EDGE,"E6.1.0.20");Q26=makeQuery(id+"F0.imprint","IMPRINT",FACE,{"disambiguationData":[TD([[makeQuery(id+"F0.imprint","IMPRINT",EDGE,{"derivedFrom":subQ1}),-1.0]])]});}
            var Q27;
            {var subQ1=sQuery(id+"F0.wireOp",EDGE,"E6.2.0.20");Q27=makeQuery(id+"F0.imprint","IMPRINT",FACE,{"disambiguationData":[TD([[makeQuery(id+"F0.imprint","IMPRINT",EDGE,{"derivedFrom":subQ1}),-1.0]])]});}
            var Q28;
            {var subQ1=sQuery(id+"F0.wireOp",EDGE,"E6.3.0.20");Q28=makeQuery(id+"F0.imprint","IMPRINT",FACE,{"disambiguationData":[TD([[makeQuery(id+"F0.imprint","IMPRINT",EDGE,{"derivedFrom":subQ1}),-1.0]])]});}
            var Q29;
            {var subQ1=sQuery(id+"F0.wireOp",EDGE,"E6.4.0.20");Q29=makeQuery(id+"F0.imprint","IMPRINT",FACE,{"disambiguationData":[TD([[makeQuery(id+"F0.imprint","IMPRINT",EDGE,{"derivedFrom":subQ1}),-1.0]])]});}
            var Q30;
            {var subQ1=sQuery(id+"F0.wireOp",EDGE,"E6.1.0.18");Q30=makeQuery(id+"F0.imprint","IMPRINT",FACE,{"disambiguationData":[TD([[makeQuery(id+"F0.imprint","IMPRINT",EDGE,{"derivedFrom":subQ1}),-1.0]])]});}
            var Q31;
            {var subQ0=sQuery(id+"F0.wireOp",EDGE,"E6.1.0.30");Q31=makeQuery(id+"F0.imprint","IMPRINT",FACE,{"disambiguationData":[TD([[makeQuery(id+"F0.imprint","IMPRINT",EDGE,{"derivedFrom":subQ0}),-1.0]])]});}
            var Q32;
            {var subQ1=sQuery(id+"F0.wireOp",EDGE,"E6.1.0.0");Q32=makeQuery(id+"F0.imprint","IMPRINT",FACE,{"disambiguationData":[TD([[makeQuery(id+"F0.imprint","IMPRINT",EDGE,{"derivedFrom":subQ1}),-1.0]])]});}
            var Q33;
            {var subQ0=sQuery(id+"F0.wireOp",EDGE,"E6.2.0.30");Q33=makeQuery(id+"F0.imprint","IMPRINT",FACE,{"disambiguationData":[TD([[makeQuery(id+"F0.imprint","IMPRINT",EDGE,{"derivedFrom":subQ0}),-1.0]])]});}
            var Q34;
            {var subQ1=sQuery(id+"F0.wireOp",EDGE,"E6.2.0.0");Q34=makeQuery(id+"F0.imprint","IMPRINT",FACE,{"disambiguationData":[TD([[makeQuery(id+"F0.imprint","IMPRINT",EDGE,{"derivedFrom":subQ1}),-1.0]])]});}
            var Q35;
            {var subQ0=sQuery(id+"F0.wireOp",EDGE,"E6.2.0.18");Q35=makeQuery(id+"F0.imprint","IMPRINT",FACE,{"disambiguationData":[TD([[makeQuery(id+"F0.imprint","IMPRINT",EDGE,{"derivedFrom":subQ0}),-1.0]])]});}
            var Q36;
            {var subQ0=sQuery(id+"F0.wireOp",EDGE,"E6.3.0.30");Q36=makeQuery(id+"F0.imprint","IMPRINT",FACE,{"disambiguationData":[TD([[makeQuery(id+"F0.imprint","IMPRINT",EDGE,{"derivedFrom":subQ0}),-1.0]])]});}
            var Q37;
            {var subQ1=sQuery(id+"F0.wireOp",EDGE,"E6.3.0.0");Q37=makeQuery(id+"F0.imprint","IMPRINT",FACE,{"disambiguationData":[TD([[makeQuery(id+"F0.imprint","IMPRINT",EDGE,{"derivedFrom":subQ1}),-1.0]])]});}
            var Q38;
            {var subQ1=sQuery(id+"F0.wireOp",EDGE,"E6.3.0.18");Q38=makeQuery(id+"F0.imprint","IMPRINT",FACE,{"disambiguationData":[TD([[makeQuery(id+"F0.imprint","IMPRINT",EDGE,{"derivedFrom":subQ1}),-1.0]])]});}
            var Q39;
            {var subQ0=sQuery(id+"F0.wireOp",EDGE,"E6.4.0.30");Q39=makeQuery(id+"F0.imprint","IMPRINT",FACE,{"disambiguationData":[TD([[makeQuery(id+"F0.imprint","IMPRINT",EDGE,{"derivedFrom":subQ0}),-1.0]])]});}
            var Q40;
            {var subQ1=sQuery(id+"F0.wireOp",EDGE,"E6.4.0.0");Q40=makeQuery(id+"F0.imprint","IMPRINT",FACE,{"disambiguationData":[TD([[makeQuery(id+"F0.imprint","IMPRINT",EDGE,{"derivedFrom":subQ1}),-1.0]])]});}
            var Q41;
            {var subQ0=sQuery(id+"F0.wireOp",EDGE,"E6.4.0.18");Q41=makeQuery(id+"F0.imprint","IMPRINT",FACE,{"disambiguationData":[TD([[makeQuery(id+"F0.imprint","IMPRINT",EDGE,{"derivedFrom":subQ0}),-1.0]])]});}
            var Q42;
            {var subQ0=sQuery(id+"F0.wireOp",EDGE,"E6.6.0.19");Q42=makeQuery(id+"F0.imprint","IMPRINT",FACE,{"disambiguationData":[TD([[makeQuery(id+"F0.imprint","IMPRINT",EDGE,{"derivedFrom":subQ0}),-1.0]])]});}
            var Q43;
            {var subQ0=sQuery(id+"F0.wireOp",EDGE,"E6.7.0.19");Q43=makeQuery(id+"F0.imprint","IMPRINT",FACE,{"disambiguationData":[TD([[makeQuery(id+"F0.imprint","IMPRINT",EDGE,{"derivedFrom":subQ0}),-1.0]])]});}
            var Q44;
            {var subQ7=sQuery(id+"F0.wireOp",EDGE,"E6.8.0.19");Q44=makeQuery(id+"F0.imprint","IMPRINT",FACE,{"disambiguationData":[TD([[makeQuery(id+"F0.imprint","IMPRINT",EDGE,{"derivedFrom":subQ7}),-1.0]])]});}
            var Q45;
            {var subQ1=sQuery(id+"F0.wireOp",EDGE,"E6.6.0.12");Q45=makeQuery(id+"F0.imprint","IMPRINT",FACE,{"disambiguationData":[TD([[makeQuery(id+"F0.imprint","IMPRINT",EDGE,{"derivedFrom":subQ1}),-1.0]])]});}
            var Q46;
            {var subQ2=sQuery(id+"F0.wireOp",EDGE,"E6.6.0.7");Q46=makeQuery(id+"F0.imprint","IMPRINT",FACE,{"disambiguationData":[TD([[makeQuery(id+"F0.imprint","IMPRINT",EDGE,{"derivedFrom":subQ2}),-1.0]])]});}
            var Q47;
            {var subQ1=sQuery(id+"F0.wireOp",EDGE,"E6.7.0.12");Q47=makeQuery(id+"F0.imprint","IMPRINT",FACE,{"disambiguationData":[TD([[makeQuery(id+"F0.imprint","IMPRINT",EDGE,{"derivedFrom":subQ1}),-1.0]])]});}
            var Q48;
            {var subQ2=sQuery(id+"F0.wireOp",EDGE,"E6.7.0.7");Q48=makeQuery(id+"F0.imprint","IMPRINT",FACE,{"disambiguationData":[TD([[makeQuery(id+"F0.imprint","IMPRINT",EDGE,{"derivedFrom":subQ2}),-1.0]])]});}
            var Q49;
            {var subQ1=sQuery(id+"F0.wireOp",EDGE,"E6.5.0.20");Q49=makeQuery(id+"F0.imprint","IMPRINT",FACE,{"disambiguationData":[TD([[makeQuery(id+"F0.imprint","IMPRINT",EDGE,{"derivedFrom":subQ1}),-1.0]])]});}
            var Q50;
            {var subQ1=sQuery(id+"F0.wireOp",EDGE,"E6.6.0.20");Q50=makeQuery(id+"F0.imprint","IMPRINT",FACE,{"disambiguationData":[TD([[makeQuery(id+"F0.imprint","IMPRINT",EDGE,{"derivedFrom":subQ1}),-1.0]])]});}
            var Q51;
            {var subQ1=sQuery(id+"F0.wireOp",EDGE,"E6.7.0.20");Q51=makeQuery(id+"F0.imprint","IMPRINT",FACE,{"disambiguationData":[TD([[makeQuery(id+"F0.imprint","IMPRINT",EDGE,{"derivedFrom":subQ1}),-1.0]])]});}
            var Q52;
            Q52=makeQuery(id+"F0.imprint","IMPRINT",FACE,{"disambiguationData":[TD([[makeQuery(id+"F0.imprint","IMPRINT",EDGE,{"derivedFrom":sQuery(id+"F0.wireOp",EDGE,"E6.9.0.2")}),-1.0]])]});
            var Q53;
            Q53=makeQuery(id+"F0.imprint","IMPRINT",FACE,{"disambiguationData":[TD([[makeQuery(id+"F0.imprint","IMPRINT",EDGE,{"derivedFrom":sQuery(id+"F0.wireOp",EDGE,"E9.0")}),-1.0]])]});
            var Q54;
            {var subQ1=sQuery(id+"F0.wireOp",EDGE,"E6.8.0.12");Q54=makeQuery(id+"F0.imprint","IMPRINT",FACE,{"disambiguationData":[TD([[makeQuery(id+"F0.imprint","IMPRINT",EDGE,{"derivedFrom":subQ1}),-1.0]])]});}
            var Q55;
            {var subQ2=sQuery(id+"F0.wireOp",EDGE,"E6.8.0.7");Q55=makeQuery(id+"F0.imprint","IMPRINT",FACE,{"disambiguationData":[TD([[makeQuery(id+"F0.imprint","IMPRINT",EDGE,{"derivedFrom":subQ2}),-1.0]])]});}
            var Q56;
            Q56=makeQuery(id+"F0.imprint","IMPRINT",FACE,{"disambiguationData":[TD([[makeQuery(id+"F0.imprint","IMPRINT",EDGE,{"derivedFrom":sQuery(id+"F0.wireOp",EDGE,"E6.9.0.7")}),-1.0]])]});
            var Q57;
            Q57=makeQuery(id+"F0.imprint","IMPRINT",FACE,{"disambiguationData":[TD([[makeQuery(id+"F0.imprint","IMPRINT",EDGE,{"derivedFrom":sQuery(id+"F0.wireOp",EDGE,"E10.0")}),-1.0]])]});
            var Q58;
            Q58=makeQuery(id+"F0.imprint","IMPRINT",FACE,{"disambiguationData":[TD([[makeQuery(id+"F0.imprint","IMPRINT",EDGE,{"derivedFrom":sQuery(id+"F0.wireOp",EDGE,"E6.8.0.13")}),-1.0]])]});
            var Q59;
            Q59=makeQuery(id+"F0.imprint","IMPRINT",FACE,{"disambiguationData":[TD([[makeQuery(id+"F0.imprint","IMPRINT",EDGE,{"derivedFrom":sQuery(id+"F0.wireOp",EDGE,"E6.9.0.13")}),-1.0]])]});
            var Q60;
            {var subQ0=sQuery(id+"F0.wireOp",EDGE,"E11.4");Q60=makeQuery(id+"F0.imprint","IMPRINT",FACE,{"disambiguationData":[TD([[makeQuery(id+"F0.imprint","IMPRINT",EDGE,{"derivedFrom":subQ0}),-1.0]])]});}
            var Q61;
            {var subQ0=sQuery(id+"F0.wireOp",EDGE,"E11.1");Q61=makeQuery(id+"F0.imprint","IMPRINT",FACE,{"disambiguationData":[TD([[makeQuery(id+"F0.imprint","IMPRINT",EDGE,{"derivedFrom":subQ0}),-1.0]])]});}
            var Q62;
            {var subQ0=sQuery(id+"F0.wireOp",EDGE,"E6.5.0.30");Q62=makeQuery(id+"F0.imprint","IMPRINT",FACE,{"disambiguationData":[TD([[makeQuery(id+"F0.imprint","IMPRINT",EDGE,{"derivedFrom":subQ0}),-1.0]])]});}
            var Q63;
            {var subQ1=sQuery(id+"F0.wireOp",EDGE,"E6.5.0.0");Q63=makeQuery(id+"F0.imprint","IMPRINT",FACE,{"disambiguationData":[TD([[makeQuery(id+"F0.imprint","IMPRINT",EDGE,{"derivedFrom":subQ1}),-1.0]])]});}
            var Q64;
            {var subQ1=sQuery(id+"F0.wireOp",EDGE,"E6.5.0.18");Q64=makeQuery(id+"F0.imprint","IMPRINT",FACE,{"disambiguationData":[TD([[makeQuery(id+"F0.imprint","IMPRINT",EDGE,{"derivedFrom":subQ1}),-1.0]])]});}
            var Q65;
            {var subQ0=sQuery(id+"F0.wireOp",EDGE,"E6.6.0.30");Q65=makeQuery(id+"F0.imprint","IMPRINT",FACE,{"disambiguationData":[TD([[makeQuery(id+"F0.imprint","IMPRINT",EDGE,{"derivedFrom":subQ0}),-1.0]])]});}
            var Q66;
            {var subQ1=sQuery(id+"F0.wireOp",EDGE,"E6.6.0.0");Q66=makeQuery(id+"F0.imprint","IMPRINT",FACE,{"disambiguationData":[TD([[makeQuery(id+"F0.imprint","IMPRINT",EDGE,{"derivedFrom":subQ1}),-1.0]])]});}
            var Q67;
            {var subQ1=sQuery(id+"F0.wireOp",EDGE,"E6.6.0.18");Q67=makeQuery(id+"F0.imprint","IMPRINT",FACE,{"disambiguationData":[TD([[makeQuery(id+"F0.imprint","IMPRINT",EDGE,{"derivedFrom":subQ1}),-1.0]])]});}
            var Q68;
            {var subQ0=sQuery(id+"F0.wireOp",EDGE,"E6.7.0.30");Q68=makeQuery(id+"F0.imprint","IMPRINT",FACE,{"disambiguationData":[TD([[makeQuery(id+"F0.imprint","IMPRINT",EDGE,{"derivedFrom":subQ0}),-1.0]])]});}
            var Q69;
            {var subQ1=sQuery(id+"F0.wireOp",EDGE,"E6.7.0.0");Q69=makeQuery(id+"F0.imprint","IMPRINT",FACE,{"disambiguationData":[TD([[makeQuery(id+"F0.imprint","IMPRINT",EDGE,{"derivedFrom":subQ1}),-1.0]])]});}
            var Q70;
            {var subQ0=sQuery(id+"F0.wireOp",EDGE,"E6.7.0.18");Q70=makeQuery(id+"F0.imprint","IMPRINT",FACE,{"disambiguationData":[TD([[makeQuery(id+"F0.imprint","IMPRINT",EDGE,{"derivedFrom":subQ0}),-1.0]])]});}
            var Q71;
            {var subQ1=sQuery(id+"F0.wireOp",EDGE,"E6.8.0.0");Q71=makeQuery(id+"F0.imprint","IMPRINT",FACE,{"disambiguationData":[TD([[makeQuery(id+"F0.imprint","IMPRINT",EDGE,{"derivedFrom":subQ1}),-1.0]])]});}
            var Q72;
            {var subQ5=sQuery(id+"F0.wireOp",EDGE,"E6.8.0.18");Q72=makeQuery(id+"F0.imprint","IMPRINT",FACE,{"disambiguationData":[TD([[makeQuery(id+"F0.imprint","IMPRINT",EDGE,{"derivedFrom":subQ5}),-1.0]])]});}
            var Q73;
            {var subQ1=sQuery(id+"F0.wireOp",EDGE,"E6.9.0.0");Q73=makeQuery(id+"F0.imprint","IMPRINT",FACE,{"disambiguationData":[TD([[makeQuery(id+"F0.imprint","IMPRINT",EDGE,{"derivedFrom":subQ1}),-1.0]])]});}
            var Q74;
            {var subQ5=sQuery(id+"F0.wireOp",EDGE,"E6.9.0.18");Q74=makeQuery(id+"F0.imprint","IMPRINT",FACE,{"disambiguationData":[TD([[makeQuery(id+"F0.imprint","IMPRINT",EDGE,{"derivedFrom":subQ5}),-1.0]])]});}
            extrude(context, id + "F1", {"entities" : qUnion([Q0, Q1, Q2, Q3, Q4, Q5, Q6, Q7, Q8, Q9, Q10, Q11, Q12, Q13, Q14, Q15, Q16, Q17, Q18, Q19, Q20, Q21, Q22, Q23, Q24, Q25, Q26, Q27, Q28, Q29, Q30, Q31, Q32, Q33, Q34, Q35, Q36, Q37, Q38, Q39, Q40, Q41, Q42, Q43, Q44, Q45, Q46, Q47, Q48, Q49, Q50, Q51, Q52, Q53, Q54, Q55, Q56, Q57, Q58, Q59, Q60, Q61, Q62, Q63, Q64, Q65, Q66, Q67, Q68, Q69, Q70, Q71, Q72, Q73, Q74]), "depth" : 1 * mm, "offsetDistance" : 25 * mm});
        }
    });
